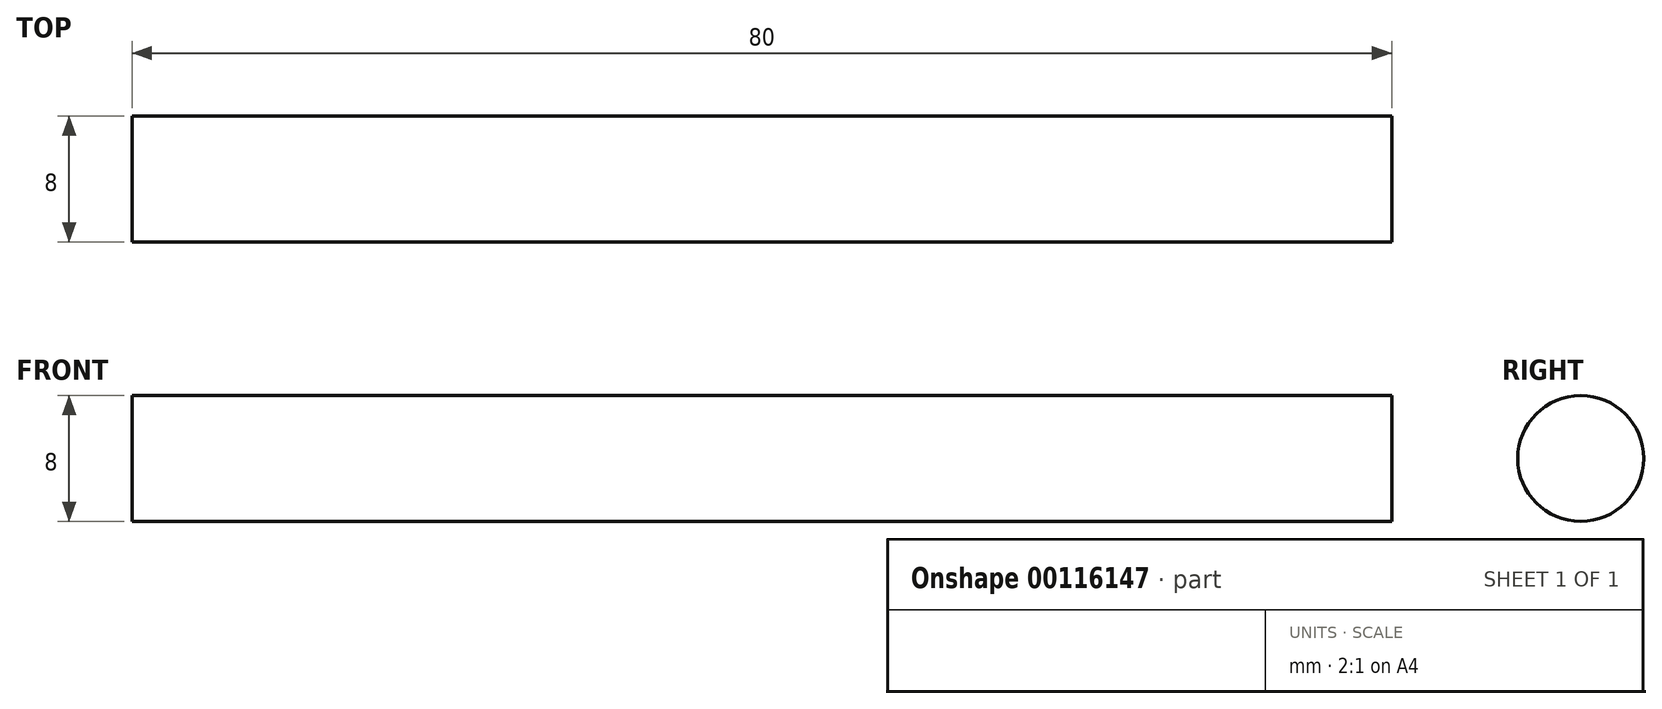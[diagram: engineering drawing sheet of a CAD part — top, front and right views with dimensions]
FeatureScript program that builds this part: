
annotation { "Feature Type Name" : "Feature", "Feature Type Description" : "" }
export const myFeature = defineFeature(function(context is Context, id is Id, definition is map)
    precondition{}
    {
        {
            var Q0;
            Q0=qCreatedBy(makeId("Right.planeOp"),FACE);
            var sketch = newSketch(context, id + "F0", { "sketchPlane" : qUnion([Q0])});
            skCircle(sketch, "E0", {"center": v(0, 0) * mm, "radius": 4 * mm});
            skSolve(sketch);
        }
        {
            var Q0;
            Q0=makeQuery(id+"F0.imprint","IMPRINT",FACE,{"disambiguationData":[TD([[makeQuery(id+"F0.imprint","IMPRINT",EDGE,{"derivedFrom":sQuery(id+"F0.wireOp",EDGE,"E0")}),1.0]])]});
            extrude(context, id + "F1", {"entities" : qUnion([Q0]), "depth" : 80 * mm});
        }
    });
